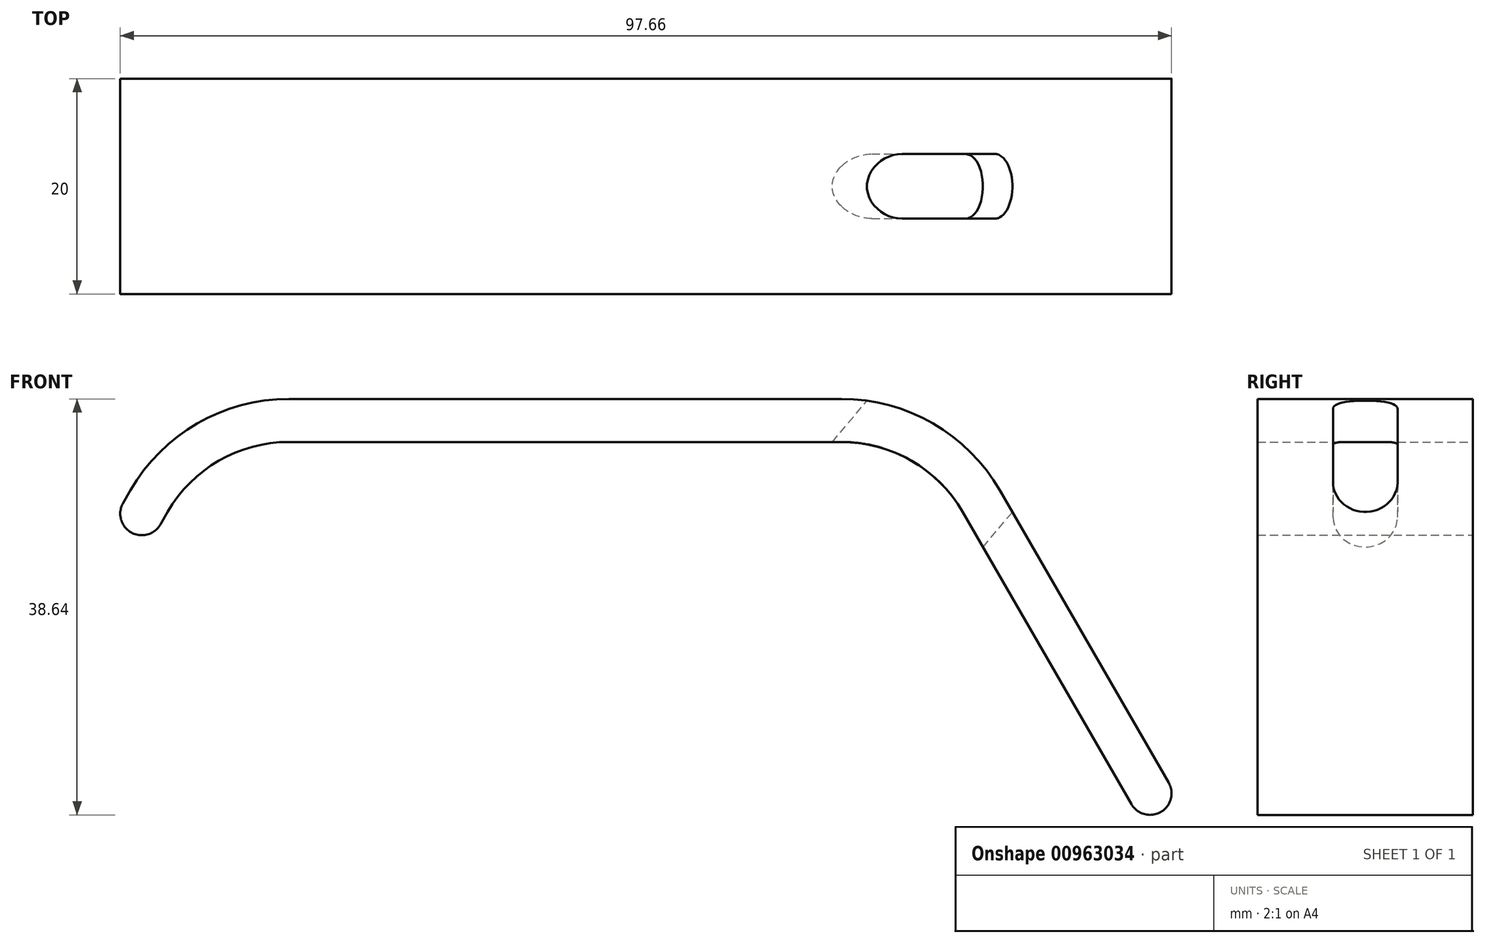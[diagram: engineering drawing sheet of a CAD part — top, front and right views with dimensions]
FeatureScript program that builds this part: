
annotation { "Feature Type Name" : "Feature", "Feature Type Description" : "" }
export const myFeature = defineFeature(function(context is Context, id is Id, definition is map)
    precondition{}
    {
        {
            var Q0;
            Q0=qCreatedBy(makeId("Front.planeOp"),FACE);
            var sketch = newSketch(context, id + "F0", { "sketchPlane" : qUnion([Q0])});
            skLineSegment(sketch, "E0", {"start": v(-8.66, 0) * mm, "end": v(-60, 0) * mm});
            skLineSegment(sketch, "E1", {"start": v(4.33, -7.5) * mm, "end": v(20, -34.64) * mm});
            skPoint(sketch, "E2.visualSharp", {"position": v(0, 0) * mm});
            skArc(sketch, "E2.filletArc", {"start": v(4.33, -7.5) * mm, "mid": v(-1.16, -2) * mm, "end": v(-8.66, 0) * mm});
            skArc(sketch, "E3.2", {"start": v(6.06, -6.5) * mm, "mid": v(-0.16, -0.28) * mm, "end": v(-8.66, 2) * mm});
            skLineSegment(sketch, "E3.3", {"start": v(6.06, -6.5) * mm, "end": v(21.73, -33.64) * mm});
            skLineSegment(sketch, "E4", {"start": v(-68.66, 0) * mm, "end": v(-68.66, 0) * mm});
            skLineSegment(sketch, "E5", {"start": v(-73, -7.5) * mm, "end": v(-73.66, -8.66) * mm});
            skPoint(sketch, "E6.visualSharp", {"position": v(-68.66, 0) * mm});
            skArc(sketch, "E6.filletArc", {"start": v(-60, 0) * mm, "mid": v(-67.5, -2) * mm, "end": v(-73, -7.5) * mm});
            skLineSegment(sketch, "E7.0", {"start": v(-74.72, -6.5) * mm, "end": v(-75.4, -7.66) * mm});
            skArc(sketch, "E7.1", {"start": v(-60, 2) * mm, "mid": v(-68.5, -0.28) * mm, "end": v(-74.72, -6.5) * mm});
            skLineSegment(sketch, "E7.2", {"start": v(-8.66, 2) * mm, "end": v(-60, 2) * mm});
            skLineSegment(sketch, "E8.0", {"start": v(-71.26, -8.5) * mm, "end": v(-71.93, -9.66) * mm});
            skArc(sketch, "E8.1", {"start": v(-60, -2) * mm, "mid": v(-66.5, -3.74) * mm, "end": v(-71.26, -8.5) * mm});
            skLineSegment(sketch, "E8.2", {"start": v(-8.66, -2) * mm, "end": v(-60, -2) * mm});
            skArc(sketch, "E9", {"start": v(-75.4, -7.66) * mm, "mid": v(-74.66, -10.4) * mm, "end": v(-71.93, -9.66) * mm});
            skArc(sketch, "E10.0", {"start": v(2.6, -8.5) * mm, "mid": v(-2.16, -3.74) * mm, "end": v(-8.66, -2) * mm});
            skLineSegment(sketch, "E10.1", {"start": v(2.6, -8.5) * mm, "end": v(18.27, -35.64) * mm});
            skArc(sketch, "E11", {"start": v(21.73, -33.64) * mm, "mid": v(21, -36.37) * mm, "end": v(18.27, -35.64) * mm});
            skSolve(sketch);
        }
        {
            var Q0;
            Q0 = qSketchRegion(id + "F0", true);
            extrude(context, id + "F1", {"entities" : qUnion([Q0]), "endBound" : BoundingType.SYMMETRIC, "depth" : 20 * mm, "offsetDistance" : 25 * mm});
        }
        {
            var Q0;
            Q0=makeQuery(id+"F1.opExtrude","SWEPT_EDGE",EDGE,{"disambiguationData":[OSD([sQuery(id+"F0.wireOp",EDGE,"E3.1"),sQuery(id+"F0.wireOp",EDGE,"E3.2")])]});
            cPlane(context, id + "F2", {"entities" : qUnion([Q0]), "cplaneType" : CPlaneType.LINE_ANGLE, "offset" : 25 * mm, "angle" : 10 * degree, "width" : 150 * mm, "height" : 150 * mm});
        }
        {
            var Q0;
            Q0=qCreatedBy(id+"F2.planeOp",FACE);
            var sketch = newSketch(context, id + "F3", { "sketchPlane" : qUnion([Q0])});
            skLineSegment(sketch, "E12", {"start": v(0, 0) * mm, "end": v(-3, 0) * mm, "construction": true});
            skLineSegment(sketch, "E13", {"start": v(0, 0) * mm, "end": v(8, 0) * mm, "construction": true});
            skArc(sketch, "E14.0.startCap", {"start": v(0, -3) * mm, "mid": v(-3, 0) * mm, "end": v(0, 3) * mm});
            skArc(sketch, "E14.0.endCap", {"start": v(8, 3) * mm, "mid": v(11, 0) * mm, "end": v(8, -3) * mm});
            skLineSegment(sketch, "E14.0.left", {"start": v(0, 3) * mm, "end": v(8, 3) * mm});
            skLineSegment(sketch, "E14.0.right", {"start": v(0, -3) * mm, "end": v(8, -3) * mm});
            skArc(sketch, "E14.1.startCap", {"start": v(0, 3) * mm, "mid": v(3, 0) * mm, "end": v(0, -3) * mm});
            skArc(sketch, "E14.1.endCap", {"start": v(-3, -3) * mm, "mid": v(-6, 0) * mm, "end": v(-3, 3) * mm});
            skLineSegment(sketch, "E14.1.left", {"start": v(0, -3) * mm, "end": v(-3, -3) * mm});
            skLineSegment(sketch, "E14.1.right", {"start": v(0, 3) * mm, "end": v(-3, 3) * mm});
            skSolve(sketch);
        }
        {
            var Q0;
            Q0 = qSketchRegion(id + "F3", true);
            extrude(context, id + "F4", {"entities" : qUnion([Q0]), "operationType" : NewBodyOperationType.REMOVE, "endBound" : BoundingType.SYMMETRIC, "oppositeDirection" : true, "depth" : 50 * mm, "offsetDistance" : 25 * mm});
        }
    });
